# Revit family: RepeatingDetail_Batten_Knotwood_25mmSuite
name_source: partatom
category: Detail Items
units: mm (PartAtom-declared; Revit-internal decimal feet)

## family parameters
Rotate with component = No
Section Shape = Not Defined
Shared = No

## types (4) — shared parameters
Manufacturer = Knotwood
ManufacturerOverallWidth = 25 mm  [stored 0.082021 ft]
ManufacturerURLProductSpecific = https://www.knotwood.com.au
ModifiedIssue = 20231110 $
URL = https://www.knotwood.com.au

## per-type parameters (varying)
| type | BattenType | Description | ManufacturerOverallDepth | ManufacturerSpecCode | Model |
| 50mm (KEB5025F) | DetailItem_Batten_Knotwood_25mmSuite : 50mm (KEB5025F) | Knotwood 25mm Batten Suite (KEB5025F) | 50 mm  [stored 0.164042 ft] | KEB5025F | KEB5025F |
| 75mm (KEB7525F) | DetailItem_Batten_Knotwood_25mmSuite : 75mm (KEB7525F) | Knotwood 25mm Batten Suite (KEB7525F) | 75 mm | KEB7525F | KEB7525F |
| 100mm (KEB10025F) | DetailItem_Batten_Knotwood_25mmSuite : 100mm (KEB10025F) | Knotwood 25mm Batten Suite (KEB10025F) | 100 mm  [stored 0.328084 ft] | KEB10025F | KEB10025F |
| 150mm (KEB15025F) | DetailItem_Batten_Knotwood_25mmSuite : 150mm (KEB15025F) | Knotwood 25mm Batten Suite (KEB15025F) | 150 mm | KEB15025F | KEB15025F |

note: [stored X ft] marks values corroborated as IEEE doubles in the binary element streams (Revit-internal decimal feet)

## geometry (parser evidence)
native form markers: Sweep x2
no freeform markers — native parametric forms only
